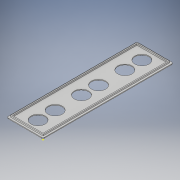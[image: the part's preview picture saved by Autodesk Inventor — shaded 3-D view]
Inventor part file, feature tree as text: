
AUTODESK INVENTOR PART (.ipt)
format: ipt  version: 2019 (Build 230136000, 136)  size: 192,512 bytes
history: native  units: mm
features: sketch x6, extrude x4, fillet x3
ambient origin geometry x8: Origin, YZ Plane, XZ Plane, XY Plane, X Axis, Y Axis, Z Axis, Center Point
bodies: Solid1 (feature_tree)
feature tree (13):
  sketch  "Sketch1"  dims[d0=51.0mm d1=183.0mm]
  extrude  "Extrusion1"  Depth=183.0mm
  extrude  "Extrusion2"  Depth=178.0mm
  sketch  "Sketch2"  dims[d2=46.0mm d3=178.0mm]
  extrude  "Extrusion3"  Depth=2.5mm
  sketch  "Sketch4"  dims[d6=2.0mm d7=0.0mm d8=4.0mm d9=0.0mm d10=43.0mm d11=175.0mm d12=1.5mm]
  sketch  "Sketch5"  dims[d13=1.5mm]
  sketch  "Sketch6"  dims[d14=2.0mm d15=0.0mm d16=20.0mm d17=20.0mm d18=20.0mm d19=20.0mm d20=20.0mm d21=20.0mm d22=5.0mm d23=0.0mm d24=2.0mm d25=1.0mm d26=1.0mm]
  extrude  "Extrusion4"  Depth=4.0mm TaperAngle=0.0deg
  fillet  "Fillet1"  Radius=43.0mm
  fillet  "Fillet2"  Radius=175.0mm
  fillet  "Fillet3"  Radius=1.5mm
  sketch  "Sketch3"  dims[d4=2.5mm d5=2.5mm]
